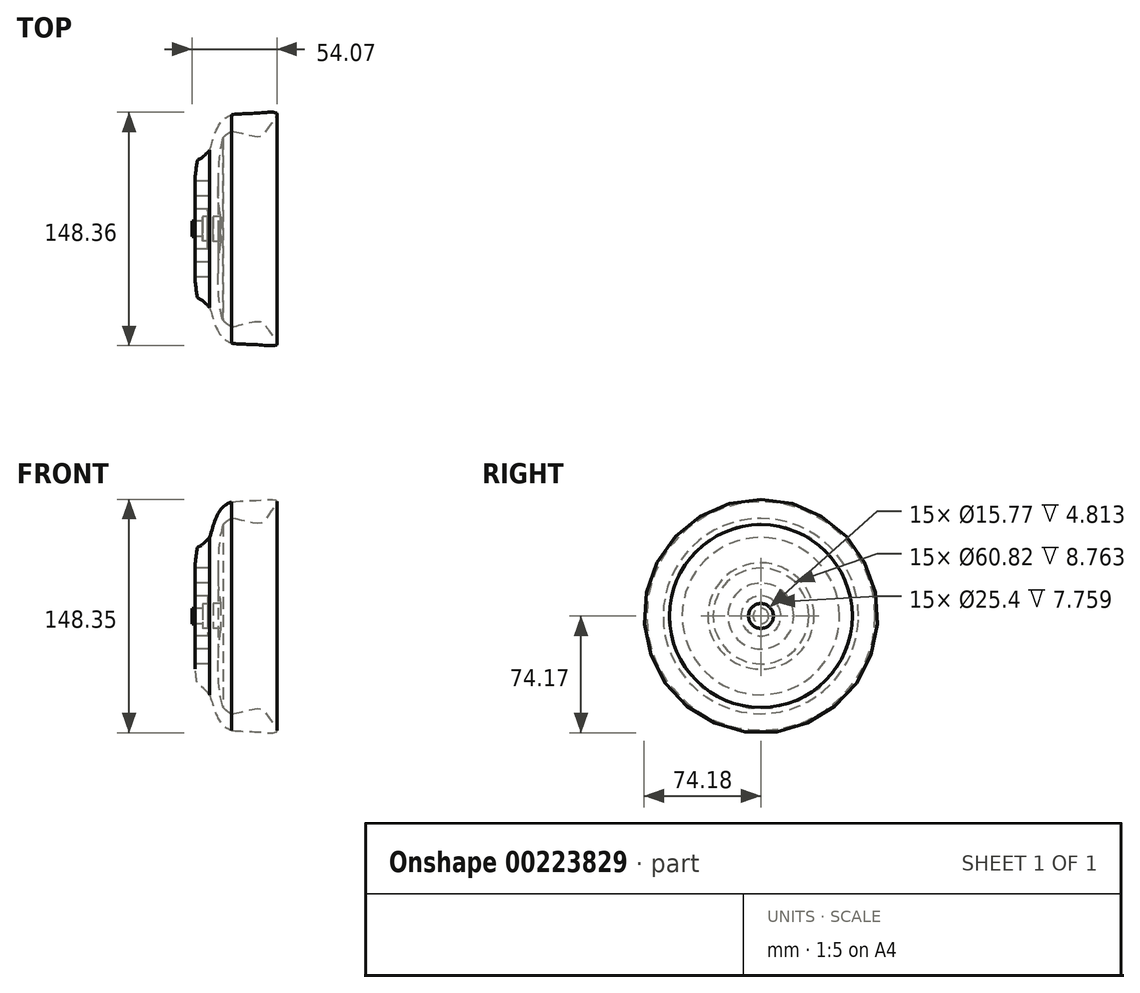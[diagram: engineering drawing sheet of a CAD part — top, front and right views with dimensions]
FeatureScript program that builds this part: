
annotation { "Feature Type Name" : "Feature", "Feature Type Description" : "" }
export const myFeature = defineFeature(function(context is Context, id is Id, definition is map)
    precondition{}
    {
        {
            var Q0;
            Q0=qCreatedBy(makeId("Front.planeOp"),FACE);
            var sketch = newSketch(context, id + "F0", { "sketchPlane" : qUnion([Q0])});
            skLineSegment(sketch, "E0", {"start": v(0, 0) * mm, "end": v(0, 4.89) * mm});
            skLineSegment(sketch, "E1", {"start": v(0, 0) * mm, "end": v(13.47, 0) * mm});
            skLineSegment(sketch, "E2", {"start": v(0, 4.89) * mm, "end": v(6.69, 4.89) * mm});
            skLineSegment(sketch, "E3", {"start": v(13.47, 0) * mm, "end": v(13.47, 7.89) * mm});
            skLineSegment(sketch, "E4", {"start": v(13.47, 7.89) * mm, "end": v(18.28, 7.89) * mm});
            skLineSegment(sketch, "E5", {"start": v(6.69, 4.89) * mm, "end": v(6.69, 7.78) * mm});
            skLineSegment(sketch, "E6", {"start": v(6.69, 7.78) * mm, "end": v(9.8, 7.78) * mm});
            skLineSegment(sketch, "E7", {"start": v(9.8, 7.78) * mm, "end": v(9.8, 12.7) * mm});
            skLineSegment(sketch, "E8", {"start": v(9.8, 12.7) * mm, "end": v(2.05, 12.7) * mm});
            skLineSegment(sketch, "E9", {"start": v(2.05, 12.7) * mm, "end": v(2.05, 20.91) * mm});
            skLineSegment(sketch, "E10", {"start": v(2.05, 20.91) * mm, "end": v(10.81, 20.91) * mm});
            skLineSegment(sketch, "E11", {"start": v(10.81, 20.91) * mm, "end": v(10.81, 30.41) * mm});
            skLineSegment(sketch, "E12", {"start": v(10.81, 30.41) * mm, "end": v(2.05, 30.41) * mm});
            skFitSpline(sketch, "E13", {"points": [v(25.04, 72.54) * mm, v(41.88, 73.6) * mm, v(53.98, 73.14) * mm, v(49, 64.76) * mm, v(42.97, 58.86) * mm, v(25.04, 62.03) * mm], "startDerivative": vector(55.9, 9.28) * mm, "endDerivative": vector(-59.8, 3.6) * mm});
            skArc(sketch, "E14", {"start": v(25.04, 62.03) * mm, "mid": v(22.27, 60.24) * mm, "end": v(19.78, 58.06) * mm});
            skLineSegment(sketch, "E15", {"start": v(2.05, 30.41) * mm, "end": v(2.05, 33.74) * mm});
            skFitSpline(sketch, "E16", {"points": [v(19.78, 58.06) * mm, v(16.72, 37.63) * mm, v(18.28, 7.89) * mm], "startDerivative": vector(-12.87, -37.04) * mm, "endDerivative": vector(11.14, -55.45) * mm});
            skFitSpline(sketch, "E17", {"points": [v(2.05, 33.74) * mm, v(3.5, 43.2) * mm, v(5.69, 44.8) * mm, v(11.28, 50) * mm], "startDerivative": vector(4.47, 10.63) * mm, "endDerivative": vector(13.6, 13.67) * mm});
            skFitSpline(sketch, "E18", {"points": [v(25.04, 72.54) * mm, v(18.46, 67.95) * mm, v(11.28, 50) * mm], "startDerivative": vector(-17.79, -8.23) * mm, "endDerivative": vector(-10.3, -34.95) * mm});
            skSolve(sketch);
        }
        {
            var Q0;
            Q0 = qSketchRegion(id + "F0", true);
            var Q1;
            Q1=sQuery(id+"F0.wireOp",EDGE,"E1");
            revolve(context, id + "F1", {"entities" : qUnion([Q0]), "axis" : qUnion([Q1]), "revolveType" : RevolveType.FULL});
        }
    });
